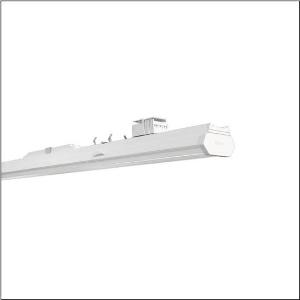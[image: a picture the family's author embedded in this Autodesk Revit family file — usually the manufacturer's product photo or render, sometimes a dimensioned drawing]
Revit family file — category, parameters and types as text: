
# Revit family: licross_r__21_protected_mo_52td11dn48xg_0db0
name_source: partatom
category: Lighting Fixtures
units: mm (PartAtom-declared; Revit-internal decimal feet)

## family parameters
Cut with Voids When Loaded = No
Host = Face
Light Source = No
Part Type = Normal
Room Calculation Point = No
Round Connector Dimension = Use Diameter
Shared = No

## types (1)
- --- (1 x LED, 8000 lm, 45.5 W, 4000K)
    Apparent Load = 46 VA
    CIE Flux Codes = 83 94 98 100 100
    Color Rendering = 80
    Color Temperature = 4000K
    Default Elevation = 1800 mm
    Description = Licross® 21 Protected MO, luminaire insert, of sheet steel, galvanised, coil coated, white, length: 1.500mm, width: 90mm, height: 103mm, LED rated luminous flux: 8.000lm, light colour: 840, SDCM (Standard Deviation of Colour Matching)MacAdam ≤ 3 SDCM (initial), control gear: DALI 2, with plug, 5-pole, with phase selection, mains connection: 220..240V, AC, 50/60Hz, rated input power: 46W, internal wiring halogen-free, primary light control with lens, of plastic, primary optical cover: cover, of PMMA, light emission: direct distribution, primary light characteristic: symmetric, protection rating (complete): IP54, insulation class (complete): insulation class I (protective earthing), certification: CE, ENEC, VDE, UKCA, protection symbol: D if used in an environment with non-conductive dust loads with corresponding accessories, impact resistance: IK06, permissible ambient temperature for indoor applications: -25..+45°C, corresponds to IFS (International Featured Standards) requirements for safety and quality in the food industry, reducing of maximum allowable ambient temperature of 5°C with ceiling mounting, LABS conformity tested according to VDMA 24364:2018-05, packaging unit: 1 piece
    Height = 92 mm
    Lamp = 1 x LED
    Lamp Light Flux = 8000 lm
    Lamp Power = 45.5 W
    Lamp count = 1
    Length = 1500 mm
    Luminous efficacy = 176 lm/W
    Manufacturer = Siteco
    ModVariant = No
    Model = 52TD11DN48XG
    Mounting Place = Ceiling
    Mounting Type = Pendant
    Number of Poles = 1
    OnlyDefault = Yes
    Power Factor = 1
    Product Name = Licross® 21 Protected MO
    Product group = luminaire insert | ceiling pendant
    ProductGroupID = 901
    Protection Class = Protection class I
    Protection Degree = IP 54
    RLX_Detail_Level = 1
    RLX_Emergency_Light_Flux = 0 lm
    RLX_Emergency_Type = 0
    RLX_Emergency_Type_DB = No
    RlxData = <blob elided: 24261 chars, md5=2c9bf764>
    Socket = socket
    Standby Power = 0 W
    System Light Flux = 8000 lm
    System Power = 46 W
    Type Comments = factory setting: luminous flux: 100 % | dim-lin: 254 | 307 mA
    Type Image = l_1256148.jpg
    URL = http://relux.com
    VarID = @adj_132207
    Voltage = 0 V
    Weight = 0.00 kg
    Width = 88 mm

## geometry (parser evidence)
native form markers: Blend x4, Sweep x10
no freeform markers — native parametric forms only
